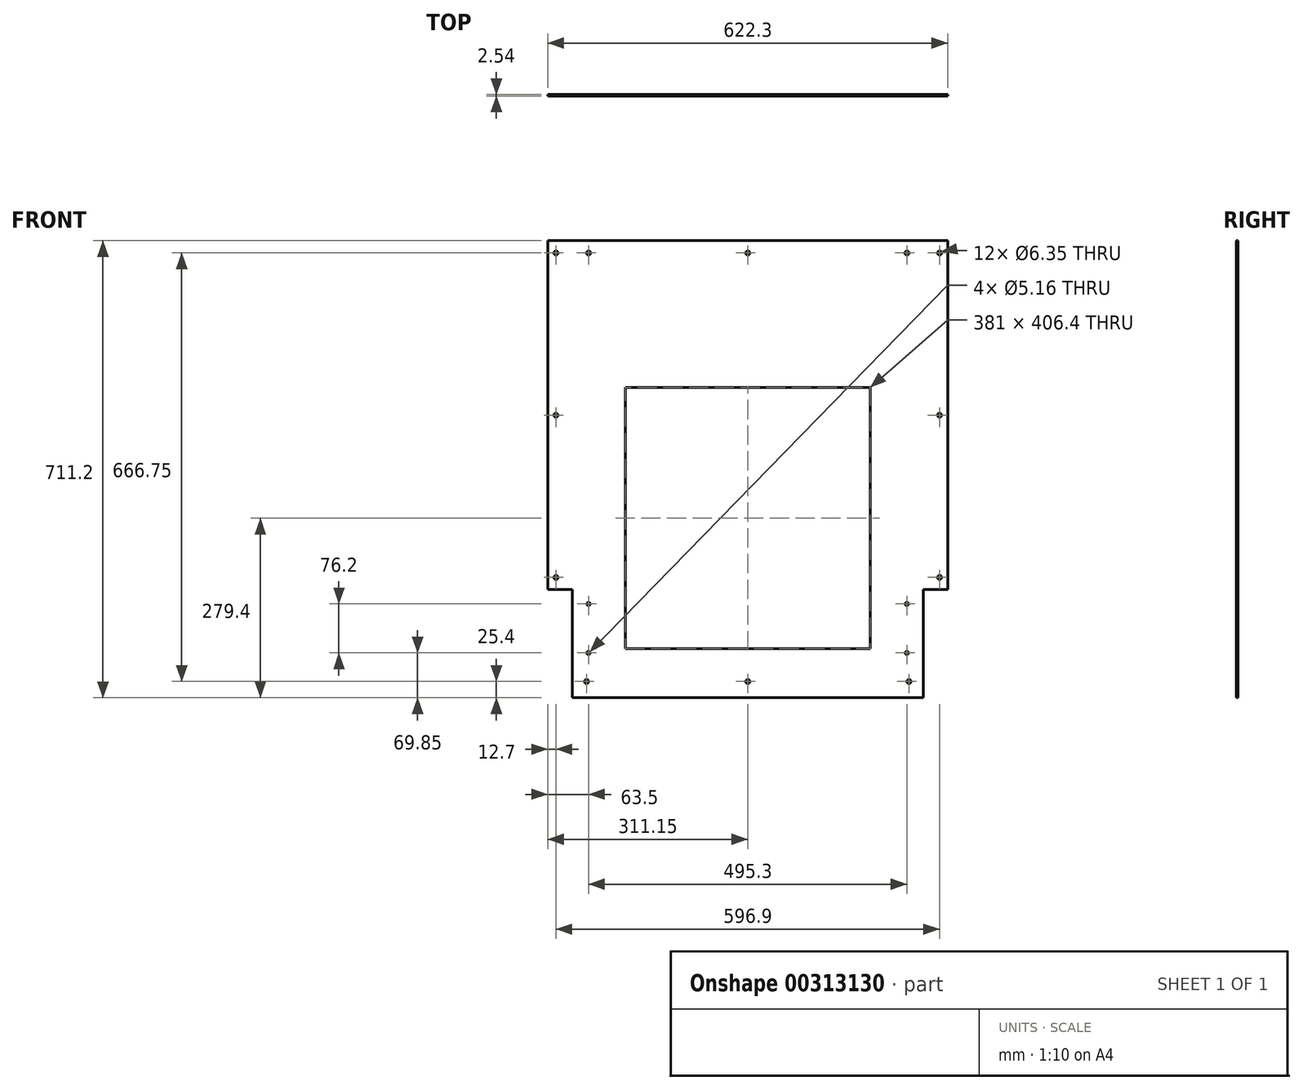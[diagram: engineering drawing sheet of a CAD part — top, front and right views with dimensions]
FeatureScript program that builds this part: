
annotation { "Feature Type Name" : "Feature", "Feature Type Description" : "" }
export const myFeature = defineFeature(function(context is Context, id is Id, definition is map)
    precondition{}
    {
        {
            var Q0;
            Q0=qCreatedBy(makeId("Front.planeOp"),FACE);
            var sketch = newSketch(context, id + "F0", { "sketchPlane" : qUnion([Q0])});
            skLineSegment(sketch, "E0.bottom", {"start": v(-311.15, 355.6) * mm, "end": v(311.15, 355.6) * mm});
            skLineSegment(sketch, "E0.top", {"start": v(-311.15, -355.6) * mm, "end": v(311.15, -355.6) * mm});
            skLineSegment(sketch, "E0.left", {"start": v(-311.15, 355.6) * mm, "end": v(-311.15, -355.6) * mm});
            skLineSegment(sketch, "E0.right", {"start": v(311.15, 355.6) * mm, "end": v(311.15, -355.6) * mm});
            skPoint(sketch, "E0.middle", {"position": v(0, 0) * mm});
            skLineSegment(sketch, "E1.bottom", {"start": v(-190.5, 127) * mm, "end": v(190.5, 127) * mm});
            skLineSegment(sketch, "E1.top", {"start": v(-190.5, -279.4) * mm, "end": v(190.5, -279.4) * mm});
            skLineSegment(sketch, "E1.left", {"start": v(-190.5, 127) * mm, "end": v(-190.5, -279.4) * mm});
            skLineSegment(sketch, "E1.right", {"start": v(190.5, 127) * mm, "end": v(190.5, -279.4) * mm});
            skPoint(sketch, "E1.middle", {"position": v(0, -76.2) * mm});
            skCircle(sketch, "E2", {"center": v(247.65, -209.55) * mm, "radius": 2.58 * mm});
            skCircle(sketch, "E3", {"center": v(247.65, -285.75) * mm, "radius": 2.58 * mm});
            skCircle(sketch, "E4", {"center": v(-247.65, -285.75) * mm, "radius": 2.58 * mm});
            skCircle(sketch, "E5", {"center": v(-247.65, -209.55) * mm, "radius": 2.58 * mm});
            skCircle(sketch, "E6", {"center": v(0, 336.55) * mm, "radius": 3.18 * mm});
            skPoint(sketch, "E6.centerSnap0", {"position": v(0, 355.6) * mm});
            skCircle(sketch, "E7", {"center": v(0, -330.2) * mm, "radius": 3.18 * mm});
            skPoint(sketch, "E7.centerSnap0", {"position": v(0, -355.6) * mm});
            skCircle(sketch, "E8", {"center": v(250.83, -330.2) * mm, "radius": 3.18 * mm});
            skCircle(sketch, "E9", {"center": v(-250.83, -330.2) * mm, "radius": 3.18 * mm});
            skLineSegment(sketch, "E10", {"start": v(-250.83, -330.2) * mm, "end": v(0, -330.2) * mm, "construction": true});
            skLineSegment(sketch, "E11", {"start": v(0, -330.2) * mm, "end": v(250.83, -330.2) * mm, "construction": true});
            skCircle(sketch, "E12", {"center": v(-298.45, 336.55) * mm, "radius": 3.17 * mm});
            skCircle(sketch, "E13", {"center": v(-298.45, 84.14) * mm, "radius": 3.17 * mm});
            skCircle(sketch, "E14", {"center": v(-298.45, -168.27) * mm, "radius": 3.17 * mm});
            skCircle(sketch, "E15", {"center": v(298.45, -168.27) * mm, "radius": 3.17 * mm});
            skCircle(sketch, "E16", {"center": v(298.45, 84.14) * mm, "radius": 3.17 * mm});
            skCircle(sketch, "E17", {"center": v(298.45, 336.55) * mm, "radius": 3.17 * mm});
            skLineSegment(sketch, "E18", {"start": v(-298.45, 336.55) * mm, "end": v(-298.45, -168.27) * mm, "construction": true});
            skLineSegment(sketch, "E19", {"start": v(298.45, -168.27) * mm, "end": v(298.45, 336.55) * mm, "construction": true});
            skCircle(sketch, "E20", {"center": v(247.65, 336.55) * mm, "radius": 3.18 * mm});
            skCircle(sketch, "E21", {"center": v(-247.65, 336.55) * mm, "radius": 3.18 * mm});
            skSolve(sketch);
        }
        {
            var Q0;
            Q0 = qSketchRegion(id + "F0", true);
            extrude(context, id + "F1", {"entities" : qUnion([Q0]), "endBound" : BoundingType.SYMMETRIC, "depth" : 2.54 * mm});
        }
        {
            var Q0;
            Q0=makeQuery(id+"F1.opExtrude","CAP_FACE",FACE,{"disambiguationData":[OSD([sQuery(id+"F0.wireOp",EDGE,"E0.bottom"),sQuery(id+"F0.wireOp",EDGE,"E0.top"),sQuery(id+"F0.wireOp",EDGE,"E0.left"),sQuery(id+"F0.wireOp",EDGE,"E0.right"),sQuery(id+"F0.wireOp",EDGE,"E1.bottom"),sQuery(id+"F0.wireOp",EDGE,"E1.top"),sQuery(id+"F0.wireOp",EDGE,"E1.left"),sQuery(id+"F0.wireOp",EDGE,"E1.right")])],"isStart":true});
            var sketch = newSketch(context, id + "F2", { "sketchPlane" : qUnion([Q0])});
            skLineSegment(sketch, "E22.bottom", {"start": v(-311.15, -355.6) * mm, "end": v(-273.05, -355.6) * mm});
            skLineSegment(sketch, "E22.top", {"start": v(-311.15, -187.32) * mm, "end": v(-273.05, -187.32) * mm});
            skLineSegment(sketch, "E22.left", {"start": v(-311.15, -355.6) * mm, "end": v(-311.15, -187.32) * mm});
            skLineSegment(sketch, "E22.right", {"start": v(-273.05, -355.6) * mm, "end": v(-273.05, -187.32) * mm});
            skLineSegment(sketch, "E23.bottom", {"start": v(311.15, -355.6) * mm, "end": v(273.05, -355.6) * mm});
            skLineSegment(sketch, "E23.top", {"start": v(311.15, -187.32) * mm, "end": v(273.05, -187.32) * mm});
            skLineSegment(sketch, "E23.left", {"start": v(311.15, -355.6) * mm, "end": v(311.15, -187.32) * mm});
            skLineSegment(sketch, "E23.right", {"start": v(273.05, -355.6) * mm, "end": v(273.05, -187.32) * mm});
            skSolve(sketch);
        }
        {
            var Q0;
            Q0 = qSketchRegion(id + "F2", true);
            extrude(context, id + "F3", {"entities" : qUnion([Q0]), "operationType" : NewBodyOperationType.REMOVE, "endBound" : BoundingType.THROUGH_ALL, "oppositeDirection" : true, "depth" : 25.4 * mm});
        }
    });
